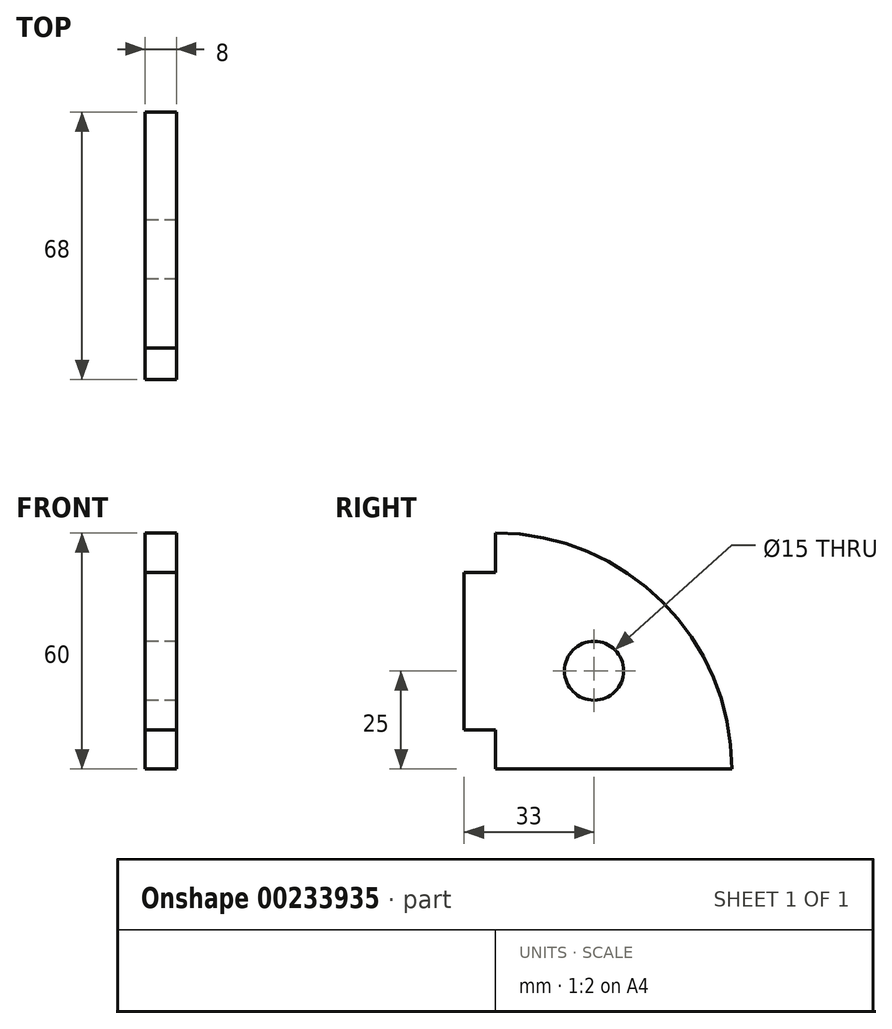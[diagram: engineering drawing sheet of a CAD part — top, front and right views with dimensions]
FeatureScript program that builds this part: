
annotation { "Feature Type Name" : "Feature", "Feature Type Description" : "" }
export const myFeature = defineFeature(function(context is Context, id is Id, definition is map)
    precondition{}
    {
        {
            var Q0;
            Q0=qCreatedBy(makeId("Right.planeOp"),FACE);
            var sketch = newSketch(context, id + "F0", { "sketchPlane" : qUnion([Q0])});
            skLineSegment(sketch, "E0", {"start": v(0, 0) * mm, "end": v(0, 10) * mm});
            skLineSegment(sketch, "E1", {"start": v(0, 10) * mm, "end": v(-8, 10) * mm});
            skLineSegment(sketch, "E2", {"start": v(-8, 10) * mm, "end": v(-8, 50) * mm});
            skLineSegment(sketch, "E3", {"start": v(-8, 50) * mm, "end": v(0, 50) * mm});
            skLineSegment(sketch, "E4", {"start": v(0, 50) * mm, "end": v(0, 60) * mm});
            skLineSegment(sketch, "E5", {"start": v(0, 0) * mm, "end": v(60, 0) * mm});
            skArc(sketch, "E6", {"start": v(0, 60) * mm, "mid": v(42.43, 42.43) * mm, "end": v(60, 0) * mm});
            skCircle(sketch, "E7", {"center": v(25, 25) * mm, "radius": 7.5 * mm});
            skSolve(sketch);
        }
        {
            var Q0;
            Q0=makeQuery(id+"F0.imprint","IMPRINT",FACE,{"disambiguationData":[TD([[makeQuery(id+"F0.imprint","IMPRINT",EDGE,{"derivedFrom":sQuery(id+"F0.wireOp",EDGE,"E0")}),-1.0]])]});
            extrude(context, id + "F1", {"entities" : qUnion([Q0]), "depth" : 8 * mm});
        }
    });
